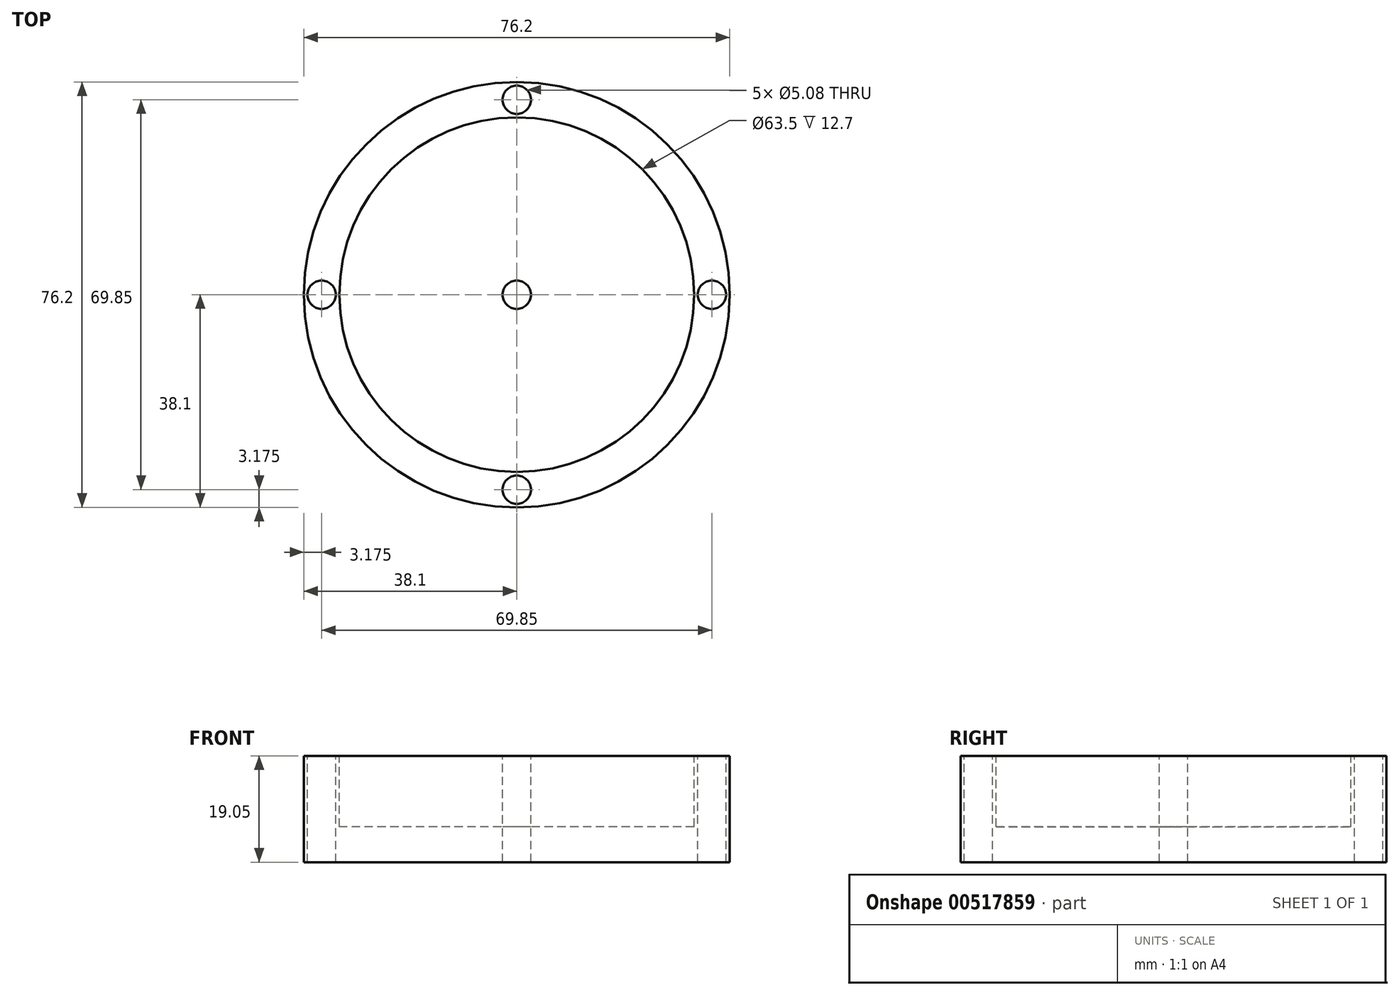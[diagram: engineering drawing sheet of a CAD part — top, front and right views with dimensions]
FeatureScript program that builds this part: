
annotation { "Feature Type Name" : "Feature", "Feature Type Description" : "" }
export const myFeature = defineFeature(function(context is Context, id is Id, definition is map)
    precondition{}
    {
        {
            var Q0;
            Q0=qCreatedBy(makeId("Right.planeOp"),FACE);
            var sketch = newSketch(context, id + "F0", { "sketchPlane" : qUnion([Q0])});
            skLineSegment(sketch, "E0", {"start": v(0, 0) * mm, "end": v(38.1, 0) * mm});
            skLineSegment(sketch, "E1", {"start": v(38.1, 0) * mm, "end": v(38.1, 19.05) * mm});
            skLineSegment(sketch, "E2", {"start": v(38.1, 19.05) * mm, "end": v(31.75, 19.05) * mm});
            skLineSegment(sketch, "E3", {"start": v(31.75, 19.05) * mm, "end": v(31.75, 6.35) * mm});
            skLineSegment(sketch, "E4", {"start": v(31.75, 6.35) * mm, "end": v(0, 6.35) * mm});
            skLineSegment(sketch, "E5", {"start": v(0, 6.35) * mm, "end": v(0, 0) * mm});
            skSolve(sketch);
        }
        {
            var Q0;
            Q0 = qSketchRegion(id + "F0", true);
            var Q1;
            Q1=sQuery(id+"F0.wireOp",EDGE,"E5");
            revolve(context, id + "F1", {"entities" : qUnion([Q0]), "axis" : qUnion([Q1]), "revolveType" : RevolveType.FULL});
        }
        {
            var Q0;
            Q0=makeQuery(id+"F1.opRevolve","SWEPT_FACE",FACE,{"disambiguationData":[OSD([sQuery(id+"F0.wireOp",EDGE,"E4")])]});
            var sketch = newSketch(context, id + "F2", { "sketchPlane" : qUnion([Q0])});
            skCircle(sketch, "E6", {"center": v(0, 0) * mm, "radius": 2.54 * mm});
            skSolve(sketch);
        }
        {
            var Q0;
            Q0 = qSketchRegion(id + "F2", true);
            extrude(context, id + "F3", {"entities" : qUnion([Q0]), "operationType" : NewBodyOperationType.REMOVE, "oppositeDirection" : true, "depth" : 25.4 * mm, "offsetDistance" : 25.4 * mm});
        }
        {
            var Q0;
            Q0=makeQuery(id+"F1.opRevolve","SWEPT_FACE",FACE,{"disambiguationData":[OSD([sQuery(id+"F0.wireOp",EDGE,"E2")])]});
            var sketch = newSketch(context, id + "F4", { "sketchPlane" : qUnion([Q0])});
            skCircle(sketch, "E7", {"center": v(0, 0) * mm, "radius": 34.93 * mm, "construction": true});
            skLineSegment(sketch, "E8", {"start": v(0, 44.31) * mm, "end": v(0, -44.31) * mm, "construction": true});
            skLineSegment(sketch, "E9", {"start": v(-43.87, 0) * mm, "end": v(45.93, 0) * mm, "construction": true});
            skCircle(sketch, "E10", {"center": v(0, 34.93) * mm, "radius": 2.54 * mm});
            skCircle(sketch, "E11", {"center": v(34.93, 0) * mm, "radius": 2.54 * mm});
            skCircle(sketch, "E12", {"center": v(-34.93, 0) * mm, "radius": 2.54 * mm});
            skCircle(sketch, "E13", {"center": v(0, -34.93) * mm, "radius": 2.54 * mm});
            skSolve(sketch);
        }
        {
            var Q0;
            Q0 = qSketchRegion(id + "F4", true);
            extrude(context, id + "F5", {"entities" : qUnion([Q0]), "operationType" : NewBodyOperationType.REMOVE, "oppositeDirection" : true, "depth" : 25.4 * mm, "offsetDistance" : 25.4 * mm});
        }
    });
